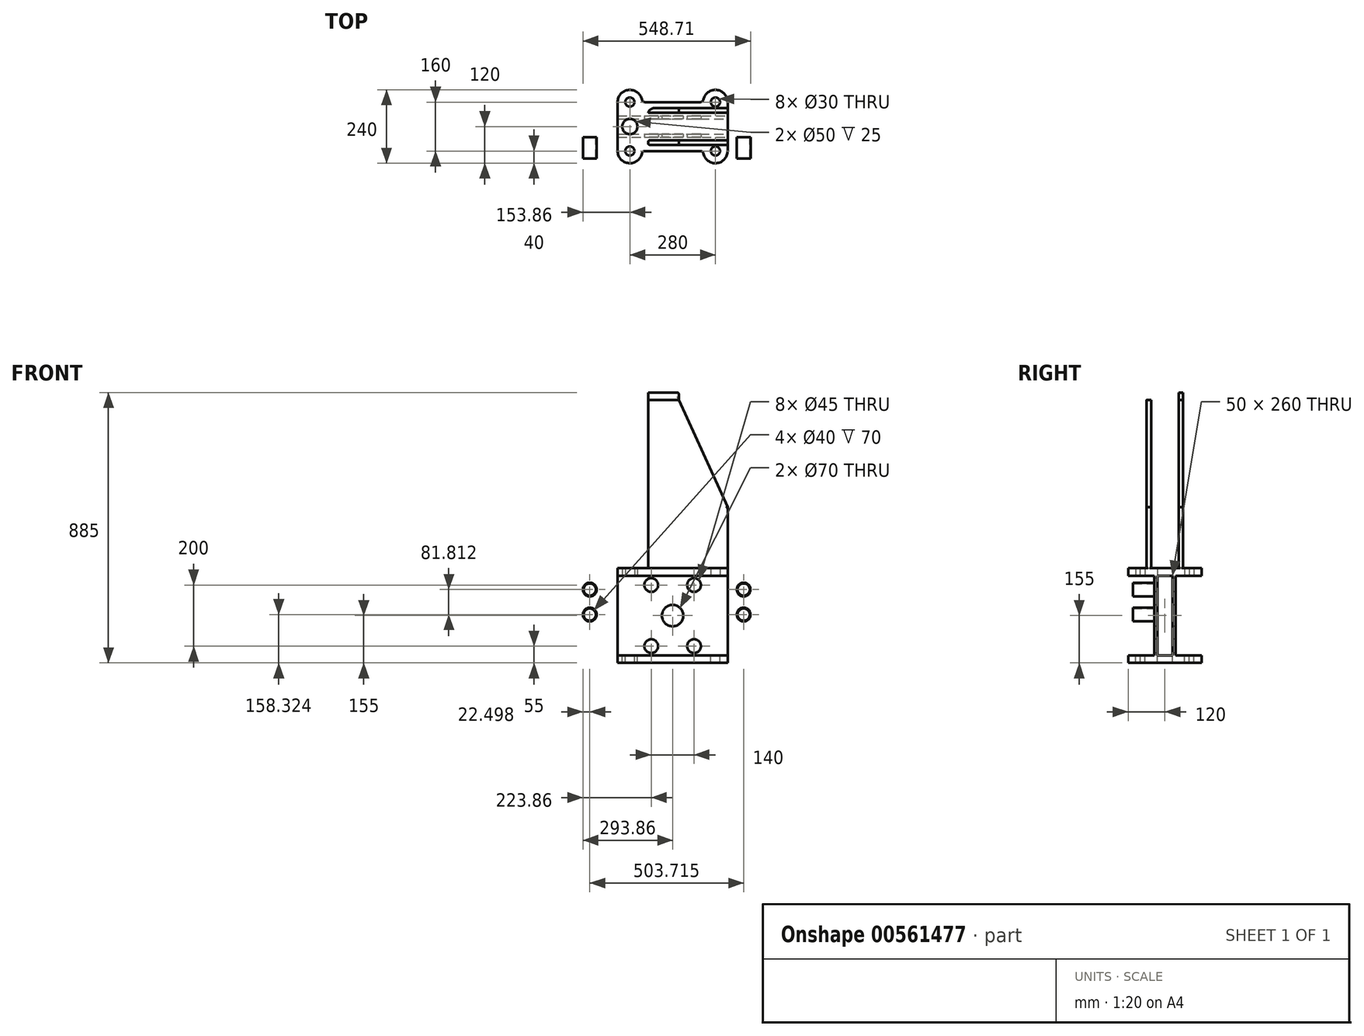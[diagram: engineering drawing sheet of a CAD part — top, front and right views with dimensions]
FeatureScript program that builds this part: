
annotation { "Feature Type Name" : "Feature", "Feature Type Description" : "" }
export const myFeature = defineFeature(function(context is Context, id is Id, definition is map)
    precondition{}
    {
        {
            var Q0;
            Q0=qCreatedBy(makeId("Top.planeOp"),FACE);
            var sketch = newSketch(context, id + "F0", { "sketchPlane" : qUnion([Q0])});
            skCircle(sketch, "E0", {"center": v(-140, 80) * mm, "radius": 40 * mm});
            skCircle(sketch, "E1", {"center": v(140, 80) * mm, "radius": 40 * mm});
            skCircle(sketch, "E2", {"center": v(-140, -80) * mm, "radius": 40 * mm});
            skCircle(sketch, "E3", {"center": v(140, -80) * mm, "radius": 40 * mm});
            skLineSegment(sketch, "E4", {"start": v(180, 80) * mm, "end": v(180, -80) * mm});
            skLineSegment(sketch, "E5", {"start": v(-180, 80) * mm, "end": v(-180, -80) * mm});
            skLineSegment(sketch, "E6", {"start": v(-100, 80) * mm, "end": v(100, 80) * mm});
            skLineSegment(sketch, "E7", {"start": v(-100, -80) * mm, "end": v(100, -80) * mm});
            skCircle(sketch, "E8", {"center": v(-140, 0) * mm, "radius": 25 * mm});
            skCircle(sketch, "E9", {"center": v(-140, 80) * mm, "radius": 15 * mm});
            skCircle(sketch, "E10", {"center": v(140, 80) * mm, "radius": 15 * mm});
            skCircle(sketch, "E11", {"center": v(-140, -80) * mm, "radius": 15 * mm});
            skCircle(sketch, "E12", {"center": v(140, -80) * mm, "radius": 15 * mm});
            skSolve(sketch);
        }
        {
            var Q0;
            {var subQ3=sQuery(id+"F0.wireOp",EDGE,"E4");Q0=makeQuery(id+"F0.imprint","IMPRINT",FACE,{"disambiguationData":[TD([[makeQuery(id+"F0.imprint","IMPRINT",EDGE,{"derivedFrom":subQ3}),-1.0]])]});}
            var Q1;
            Q1=makeQuery(id+"F0.imprint","IMPRINT",FACE,{"disambiguationData":[TD([[makeQuery(id+"F0.imprint","IMPRINT",EDGE,{"derivedFrom":sQuery(id+"F0.wireOp",EDGE,"E9")}),-1.0]])]});
            var Q2;
            Q2=makeQuery(id+"F0.imprint","IMPRINT",FACE,{"disambiguationData":[TD([[makeQuery(id+"F0.imprint","IMPRINT",EDGE,{"derivedFrom":sQuery(id+"F0.wireOp",EDGE,"E10")}),-1.0]])]});
            var Q3;
            Q3=makeQuery(id+"F0.imprint","IMPRINT",FACE,{"disambiguationData":[TD([[makeQuery(id+"F0.imprint","IMPRINT",EDGE,{"derivedFrom":sQuery(id+"F0.wireOp",EDGE,"E12")}),-1.0]])]});
            var Q4;
            Q4=makeQuery(id+"F0.imprint","IMPRINT",FACE,{"disambiguationData":[TD([[makeQuery(id+"F0.imprint","IMPRINT",EDGE,{"derivedFrom":sQuery(id+"F0.wireOp",EDGE,"E11")}),-1.0]])]});
            extrude(context, id + "F1", {"entities" : qUnion([Q0, Q1, Q2, Q3, Q4]), "depth" : 25 * mm, "offsetDistance" : 25 * mm});
        }
        {
            var Q0;
            Q0=makeQuery(id+"F1.opExtrude","SWEPT_EDGE",EDGE,{"disambiguationData":[OSD([sQuery(id+"F0.wireOp",EDGE,"E0"),sQuery(id+"F0.wireOp",EDGE,"E6")])]});
            var Q1;
            Q1=makeQuery(id+"F1.opExtrude","SWEPT_EDGE",EDGE,{"disambiguationData":[OSD([sQuery(id+"F0.wireOp",EDGE,"E1"),sQuery(id+"F0.wireOp",EDGE,"E6")])]});
            var Q2;
            Q2=makeQuery(id+"F1.opExtrude","SWEPT_EDGE",EDGE,{"disambiguationData":[OSD([sQuery(id+"F0.wireOp",EDGE,"E3"),sQuery(id+"F0.wireOp",EDGE,"E7")])]});
            var Q3;
            Q3=makeQuery(id+"F1.opExtrude","SWEPT_EDGE",EDGE,{"disambiguationData":[OSD([sQuery(id+"F0.wireOp",EDGE,"E2"),sQuery(id+"F0.wireOp",EDGE,"E7")])]});
            fillet(context, id + "F2", {"entities" : qUnion([Q0, Q1, Q2, Q3]), "radius" : 10 * mm, "tangentPropagation" : true, "allowEdgeOverflow" : false});
        }
        {
            var Q0;
            Q0=makeQuery(id+"F1.opExtrude","CAP_FACE",FACE,{"disambiguationData":[OSD([sQuery(id+"F0.wireOp",EDGE,"E0"),sQuery(id+"F0.wireOp",EDGE,"E1"),sQuery(id+"F0.wireOp",EDGE,"E2"),sQuery(id+"F0.wireOp",EDGE,"E3"),sQuery(id+"F0.wireOp",EDGE,"E4"),sQuery(id+"F0.wireOp",EDGE,"E5"),sQuery(id+"F0.wireOp",EDGE,"E6"),sQuery(id+"F0.wireOp",EDGE,"E7"),sQuery(id+"F0.wireOp",EDGE,"E8"),sQuery(id+"F0.wireOp",EDGE,"E9"),sQuery(id+"F0.wireOp",EDGE,"E10"),sQuery(id+"F0.wireOp",EDGE,"E11"),sQuery(id+"F0.wireOp",EDGE,"E12")])],"isStart":true});
            var sketch = newSketch(context, id + "F3", { "sketchPlane" : qUnion([Q0])});
            skLineSegment(sketch, "E13.bottom", {"start": v(-180, 25) * mm, "end": v(180, 25) * mm});
            skLineSegment(sketch, "E13.top", {"start": v(-180, 35) * mm, "end": v(180, 35) * mm});
            skLineSegment(sketch, "E13.left", {"start": v(-180, 25) * mm, "end": v(-180, 35) * mm});
            skLineSegment(sketch, "E13.right", {"start": v(180, 25) * mm, "end": v(180, 35) * mm});
            skLineSegment(sketch, "E14.bottom", {"start": v(-180, -25) * mm, "end": v(180, -25) * mm});
            skLineSegment(sketch, "E14.top", {"start": v(-180, -35) * mm, "end": v(180, -35) * mm});
            skLineSegment(sketch, "E14.left", {"start": v(-180, -25) * mm, "end": v(-180, -35) * mm});
            skLineSegment(sketch, "E14.right", {"start": v(180, -25) * mm, "end": v(180, -35) * mm});
            skSolve(sketch);
        }
        {
            var Q0;
            Q0=makeQuery(id+"F3.imprint","IMPRINT",FACE,{"disambiguationData":[TD([[makeQuery(id+"F3.imprint","IMPRINT",EDGE,{"derivedFrom":sQuery(id+"F3.wireOp",EDGE,"E13.top")}),-1.0]])]});
            var Q1;
            Q1=makeQuery(id+"F3.imprint","IMPRINT",FACE,{"disambiguationData":[TD([[makeQuery(id+"F3.imprint","IMPRINT",EDGE,{"derivedFrom":sQuery(id+"F3.wireOp",EDGE,"E14.top")}),1.0]])]});
            extrude(context, id + "F4", {"entities" : qUnion([Q0, Q1]), "operationType" : NewBodyOperationType.ADD, "depth" : 260 * mm, "offsetDistance" : 25 * mm});
        }
        {
            var Q0;
            Q0=makeQuery(id+"F4.opExtrude","CAP_FACE",FACE,{"disambiguationData":[OSD([sQuery(id+"F3.wireOp",EDGE,"E13.bottom"),sQuery(id+"F3.wireOp",EDGE,"E13.top"),sQuery(id+"F3.wireOp",EDGE,"E13.left"),sQuery(id+"F3.wireOp",EDGE,"E13.right")])],"isStart":false});
            var sketch = newSketch(context, id + "F5", { "sketchPlane" : qUnion([Q0])});
            skLineSegment(sketch, "E15.0", {"start": v(-180, 35) * mm, "end": v(-180, 80) * mm});
            skArc(sketch, "E16.0", {"start": v(-180, 80) * mm, "mid": v(-144.02, 119.8) * mm, "end": v(-100.8, 88) * mm});
            skLineSegment(sketch, "E17.0", {"start": v(-91.01, 80) * mm, "end": v(91.01, 80) * mm});
            skLineSegment(sketch, "E18.0.0", {"start": v(-180, 80) * mm, "end": v(-180, 35) * mm});
            skLineSegment(sketch, "E18.0.1", {"start": v(-180, 35) * mm, "end": v(180, 35) * mm});
            skLineSegment(sketch, "E18.0.2", {"start": v(180, 35) * mm, "end": v(180, 80) * mm});
            skArc(sketch, "E18.0.3", {"start": v(180, 80) * mm, "mid": v(144.02, 119.8) * mm, "end": v(100.8, 88) * mm});
            skArc(sketch, "E18.0.4", {"start": v(100.8, 88) * mm, "mid": v(97.33, 82.25) * mm, "end": v(91.01, 80) * mm});
            skLineSegment(sketch, "E18.0.5", {"start": v(91.01, 80) * mm, "end": v(-91.01, 80) * mm});
            skArc(sketch, "E18.0.6", {"start": v(-91.01, 80) * mm, "mid": v(-97.33, 82.25) * mm, "end": v(-100.8, 88) * mm});
            skArc(sketch, "E18.0.7", {"start": v(-100.8, 88) * mm, "mid": v(-144.02, 119.8) * mm, "end": v(-180, 80) * mm});
            skLineSegment(sketch, "E19.0.0", {"start": v(180, -35) * mm, "end": v(-180, -35) * mm});
            skLineSegment(sketch, "E19.0.1", {"start": v(-180, -35) * mm, "end": v(-180, -80) * mm});
            skArc(sketch, "E19.0.2", {"start": v(-180, -80) * mm, "mid": v(-144.02, -119.8) * mm, "end": v(-100.8, -88) * mm});
            skArc(sketch, "E19.0.3", {"start": v(-100.8, -88) * mm, "mid": v(-97.33, -82.25) * mm, "end": v(-91.01, -80) * mm});
            skLineSegment(sketch, "E19.0.4", {"start": v(-91.01, -80) * mm, "end": v(91.01, -80) * mm});
            skArc(sketch, "E19.0.5", {"start": v(91.01, -80) * mm, "mid": v(97.33, -82.25) * mm, "end": v(100.8, -88) * mm});
            skArc(sketch, "E19.0.6", {"start": v(100.8, -88) * mm, "mid": v(144.02, -119.8) * mm, "end": v(180, -80) * mm});
            skLineSegment(sketch, "E19.0.7", {"start": v(180, -80) * mm, "end": v(180, -35) * mm});
            skArc(sketch, "E20.0.0", {"start": v(-140, 25) * mm, "mid": v(-115, 0) * mm, "end": v(-140, -25) * mm});
            skLineSegment(sketch, "E20.0.1", {"start": v(-140, -25) * mm, "end": v(180, -25) * mm});
            skLineSegment(sketch, "E20.0.2", {"start": v(180, -25) * mm, "end": v(180, 25) * mm});
            skLineSegment(sketch, "E20.0.3", {"start": v(180, 25) * mm, "end": v(-140, 25) * mm});
            skLineSegment(sketch, "E21.0.0", {"start": v(-180, 25) * mm, "end": v(-180, -25) * mm});
            skLineSegment(sketch, "E21.0.1", {"start": v(-180, -25) * mm, "end": v(-140, -25) * mm});
            skArc(sketch, "E21.0.2", {"start": v(-140, -25) * mm, "mid": v(-165, 0) * mm, "end": v(-140, 25) * mm});
            skLineSegment(sketch, "E21.0.3", {"start": v(-140, 25) * mm, "end": v(-180, 25) * mm});
            skLineSegment(sketch, "E22.0.0", {"start": v(180, 35) * mm, "end": v(-180, 35) * mm});
            skLineSegment(sketch, "E22.0.1", {"start": v(-180, 35) * mm, "end": v(-180, 25) * mm});
            skLineSegment(sketch, "E22.0.2", {"start": v(-180, 25) * mm, "end": v(180, 25) * mm});
            skLineSegment(sketch, "E22.0.3", {"start": v(180, 25) * mm, "end": v(180, 35) * mm});
            skLineSegment(sketch, "E23.0.0", {"start": v(-180, -25) * mm, "end": v(-180, -35) * mm});
            skLineSegment(sketch, "E23.0.1", {"start": v(-180, -35) * mm, "end": v(180, -35) * mm});
            skLineSegment(sketch, "E23.0.2", {"start": v(180, -35) * mm, "end": v(180, -25) * mm});
            skLineSegment(sketch, "E23.0.3", {"start": v(180, -25) * mm, "end": v(-180, -25) * mm});
            skCircle(sketch, "E24", {"center": v(-140, 80) * mm, "radius": 15 * mm});
            skCircle(sketch, "E25", {"center": v(140, 80) * mm, "radius": 15 * mm});
            skCircle(sketch, "E26", {"center": v(140, -80) * mm, "radius": 15 * mm});
            skCircle(sketch, "E27", {"center": v(-140, -80) * mm, "radius": 15 * mm});
            skSolve(sketch);
        }
        {
            var Q0;
            Q0 = qSketchRegion(id + "F5", true);
            extrude(context, id + "F6", {"entities" : qUnion([Q0]), "operationType" : NewBodyOperationType.ADD, "depth" : 25 * mm, "offsetDistance" : 25 * mm});
        }
        {
            var Q0;
            Q0=makeQuery(id+"F4.opExtrude","SWEPT_FACE",FACE,{"disambiguationData":[OSD([sQuery(id+"F3.wireOp",EDGE,"E13.top")])]});
            var sketch = newSketch(context, id + "F7", { "sketchPlane" : qUnion([Q0])});
            skLineSegment(sketch, "E28", {"start": v(0, 0) * mm, "end": v(0, -293.43) * mm, "construction": true});
            skPoint(sketch, "E28.endSnap0", {"position": v(0, -260) * mm});
            skCircle(sketch, "E29", {"center": v(-70, -30) * mm, "radius": 22.5 * mm});
            skCircle(sketch, "E30", {"center": v(70, -30) * mm, "radius": 22.5 * mm});
            skCircle(sketch, "E31", {"center": v(-70, -230) * mm, "radius": 22.5 * mm});
            skCircle(sketch, "E32", {"center": v(70, -230) * mm, "radius": 22.5 * mm});
            skCircle(sketch, "E33", {"center": v(0, -130) * mm, "radius": 35 * mm});
            skSolve(sketch);
        }
        {
            var Q0;
            Q0=makeQuery(id+"F7.imprint","IMPRINT",FACE,{"disambiguationData":[TD([[makeQuery(id+"F7.imprint","IMPRINT",EDGE,{"derivedFrom":sQuery(id+"F7.wireOp",EDGE,"E29")}),1.0]])]});
            var Q1;
            Q1=makeQuery(id+"F7.imprint","IMPRINT",FACE,{"disambiguationData":[TD([[makeQuery(id+"F7.imprint","IMPRINT",EDGE,{"derivedFrom":sQuery(id+"F7.wireOp",EDGE,"E30")}),1.0]])]});
            var Q2;
            Q2=makeQuery(id+"F7.imprint","IMPRINT",FACE,{"disambiguationData":[TD([[makeQuery(id+"F7.imprint","IMPRINT",EDGE,{"derivedFrom":sQuery(id+"F7.wireOp",EDGE,"E33")}),1.0]])]});
            var Q3;
            Q3=makeQuery(id+"F7.imprint","IMPRINT",FACE,{"disambiguationData":[TD([[makeQuery(id+"F7.imprint","IMPRINT",EDGE,{"derivedFrom":sQuery(id+"F7.wireOp",EDGE,"E32")}),1.0]])]});
            var Q4;
            Q4=makeQuery(id+"F7.imprint","IMPRINT",FACE,{"disambiguationData":[TD([[makeQuery(id+"F7.imprint","IMPRINT",EDGE,{"derivedFrom":sQuery(id+"F7.wireOp",EDGE,"E31")}),1.0]])]});
            extrude(context, id + "F8", {"entities" : qUnion([Q0, Q1, Q2, Q3, Q4]), "operationType" : NewBodyOperationType.REMOVE, "oppositeDirection" : true, "depth" : 70 * mm, "offsetDistance" : 25 * mm});
        }
        {
            var Q0;
            Q0=makeQuery(id+"F4.opExtrude","SWEPT_FACE",FACE,{"disambiguationData":[OSD([sQuery(id+"F3.wireOp",EDGE,"E13.top")])]});
            var sketch = newSketch(context, id + "F9", { "sketchPlane" : qUnion([Q0])});
            skCircle(sketch, "E34", {"center": v(-271.36, -44.86) * mm, "radius": 22.5 * mm});
            skCircle(sketch, "E35", {"center": v(-271.36, -44.86) * mm, "radius": 20 * mm});
            skCircle(sketch, "E36", {"center": v(-271.36, -126.68) * mm, "radius": 22.5 * mm});
            skCircle(sketch, "E37", {"center": v(-271.36, -126.68) * mm, "radius": 20 * mm});
            skCircle(sketch, "E38", {"center": v(232.35, -44.86) * mm, "radius": 22.5 * mm});
            skCircle(sketch, "E39", {"center": v(232.35, -44.86) * mm, "radius": 20 * mm});
            skCircle(sketch, "E40", {"center": v(232.35, -126.68) * mm, "radius": 22.5 * mm});
            skCircle(sketch, "E41", {"center": v(232.35, -126.68) * mm, "radius": 20 * mm});
            skSolve(sketch);
        }
        {
            var Q0;
            Q0=makeQuery(id+"F9.imprint","IMPRINT",FACE,{"disambiguationData":[TD([[makeQuery(id+"F9.imprint","IMPRINT",EDGE,{"derivedFrom":sQuery(id+"F9.wireOp",EDGE,"E34")}),1.0]])]});
            var Q1;
            Q1=makeQuery(id+"F9.imprint","IMPRINT",FACE,{"disambiguationData":[TD([[makeQuery(id+"F9.imprint","IMPRINT",EDGE,{"derivedFrom":sQuery(id+"F9.wireOp",EDGE,"E36")}),1.0]])]});
            var Q2;
            Q2=makeQuery(id+"F9.imprint","IMPRINT",FACE,{"disambiguationData":[TD([[makeQuery(id+"F9.imprint","IMPRINT",EDGE,{"derivedFrom":sQuery(id+"F9.wireOp",EDGE,"E38")}),1.0]])]});
            var Q3;
            Q3=makeQuery(id+"F9.imprint","IMPRINT",FACE,{"disambiguationData":[TD([[makeQuery(id+"F9.imprint","IMPRINT",EDGE,{"derivedFrom":sQuery(id+"F9.wireOp",EDGE,"E40")}),1.0]])]});
            extrude(context, id + "F10", {"entities" : qUnion([Q0, Q1, Q2, Q3]), "depth" : 70 * mm, "offsetDistance" : 25 * mm});
        }
        {
            var Q0;
            Q0=makeQuery(id+"F1.opExtrude","CAP_FACE",FACE,{"disambiguationData":[OSD([sQuery(id+"F0.wireOp",EDGE,"E0"),sQuery(id+"F0.wireOp",EDGE,"E1"),sQuery(id+"F0.wireOp",EDGE,"E2"),sQuery(id+"F0.wireOp",EDGE,"E3"),sQuery(id+"F0.wireOp",EDGE,"E4"),sQuery(id+"F0.wireOp",EDGE,"E5"),sQuery(id+"F0.wireOp",EDGE,"E6"),sQuery(id+"F0.wireOp",EDGE,"E7"),sQuery(id+"F0.wireOp",EDGE,"E8"),sQuery(id+"F0.wireOp",EDGE,"E9"),sQuery(id+"F0.wireOp",EDGE,"E10"),sQuery(id+"F0.wireOp",EDGE,"E11"),sQuery(id+"F0.wireOp",EDGE,"E12")])],"isStart":false});
            var sketch = newSketch(context, id + "F11", { "sketchPlane" : qUnion([Q0])});
            skLineSegment(sketch, "E42.bottom", {"start": v(180, 60) * mm, "end": v(-80, 60) * mm});
            skLineSegment(sketch, "E42.top", {"start": v(180, 45) * mm, "end": v(-80, 45) * mm});
            skLineSegment(sketch, "E42.left", {"start": v(180, 60) * mm, "end": v(180, 45) * mm});
            skLineSegment(sketch, "E42.right", {"start": v(-80, 60) * mm, "end": v(-80, 45) * mm});
            skLineSegment(sketch, "E43.bottom", {"start": v(180, -60) * mm, "end": v(-80, -60) * mm});
            skLineSegment(sketch, "E43.top", {"start": v(180, -45) * mm, "end": v(-80, -45) * mm});
            skLineSegment(sketch, "E43.left", {"start": v(180, -60) * mm, "end": v(180, -45) * mm});
            skLineSegment(sketch, "E43.right", {"start": v(-80, -60) * mm, "end": v(-80, -45) * mm});
            skSolve(sketch);
        }
        {
            var Q0;
            Q0=makeQuery(id+"F11.imprint","IMPRINT",FACE,{"disambiguationData":[TD([[makeQuery(id+"F11.imprint","IMPRINT",EDGE,{"derivedFrom":sQuery(id+"F11.wireOp",EDGE,"E42.bottom")}),1.0]])]});
            var Q1;
            Q1=makeQuery(id+"F11.imprint","IMPRINT",FACE,{"disambiguationData":[TD([[makeQuery(id+"F11.imprint","IMPRINT",EDGE,{"derivedFrom":sQuery(id+"F11.wireOp",EDGE,"E43.bottom")}),-1.0]])]});
            extrude(context, id + "F12", {"entities" : qUnion([Q0, Q1]), "operationType" : NewBodyOperationType.ADD, "depth" : 550 * mm, "offsetDistance" : 25 * mm});
        }
        {
            var Q0;
            Q0=makeQuery(id+"F12.opExtrude","SWEPT_FACE",FACE,{"disambiguationData":[OSD([sQuery(id+"F11.wireOp",EDGE,"E43.bottom")])]});
            var sketch = newSketch(context, id + "F13", { "sketchPlane" : qUnion([Q0])});
            skLineSegment(sketch, "E44", {"start": v(20, 575) * mm, "end": v(180, 225) * mm});
            skSolve(sketch);
        }
        {
            var Q0;
            {var subQ0=sQuery(id+"F13.wireOp",EDGE,"E44");Q0=makeQuery(id+"F13.imprint","IMPRINT",FACE,{"disambiguationData":[TD([[makeQuery(id+"F13.imprint","IMPRINT",EDGE,{"derivedFrom":subQ0}),1.0]])]});}
            extrude(context, id + "F14", {"entities" : qUnion([Q0]), "operationType" : NewBodyOperationType.REMOVE, "endBound" : BoundingType.SYMMETRIC, "depth" : 70 * mm, "offsetDistance" : 25 * mm});
        }
        {
            var Q0;
            Q0=makeQuery(id+"F12.opExtrude","SWEPT_FACE",FACE,{"disambiguationData":[OSD([sQuery(id+"F11.wireOp",EDGE,"E42.bottom")])]});
            var sketch = newSketch(context, id + "F15", { "sketchPlane" : qUnion([Q0])});
            skLineSegment(sketch, "E45", {"start": v(-20, 575) * mm, "end": v(-180, 225) * mm});
            skSolve(sketch);
        }
        {
            var Q0;
            {var subQ0=sQuery(id+"F15.wireOp",EDGE,"E45");Q0=makeQuery(id+"F15.imprint","IMPRINT",FACE,{"disambiguationData":[TD([[makeQuery(id+"F15.imprint","IMPRINT",EDGE,{"derivedFrom":subQ0}),-1.0]])]});}
            extrude(context, id + "F16", {"entities" : qUnion([Q0]), "operationType" : NewBodyOperationType.REMOVE, "oppositeDirection" : true, "depth" : 70 * mm, "offsetDistance" : 25 * mm});
        }
        {
            var Q0;
            Q0=makeQuery(id+"F12.opExtrude","CAP_FACE",FACE,{"disambiguationData":[OSD([sQuery(id+"F11.wireOp",EDGE,"E42.bottom"),sQuery(id+"F11.wireOp",EDGE,"E42.top"),sQuery(id+"F11.wireOp",EDGE,"E42.left"),sQuery(id+"F11.wireOp",EDGE,"E42.right")])],"isStart":false});
            var sketch = newSketch(context, id + "F17", { "sketchPlane" : qUnion([Q0])});
            skLineSegment(sketch, "E46.1.0", {"start": v(-80, -60) * mm, "end": v(20, -60) * mm});
            skLineSegment(sketch, "E46.1.1", {"start": v(20, -60) * mm, "end": v(20, -45) * mm});
            skLineSegment(sketch, "E46.1.2", {"start": v(20, -45) * mm, "end": v(-80, -45) * mm});
            skLineSegment(sketch, "E46.1.3", {"start": v(-80, -45) * mm, "end": v(-80, -60) * mm});
            skLineSegment(sketch, "E46.2.0", {"start": v(180, -80) * mm, "end": v(180, -60) * mm});
            skLineSegment(sketch, "E46.2.1", {"start": v(180, -60) * mm, "end": v(-80, -60) * mm});
            skLineSegment(sketch, "E46.2.2", {"start": v(-80, -60) * mm, "end": v(-80, -45) * mm});
            skLineSegment(sketch, "E46.2.3", {"start": v(-80, -45) * mm, "end": v(180, -45) * mm});
            skLineSegment(sketch, "E46.2.4", {"start": v(180, -45) * mm, "end": v(180, 45) * mm});
            skLineSegment(sketch, "E46.2.5", {"start": v(180, 45) * mm, "end": v(-80, 45) * mm});
            skLineSegment(sketch, "E46.2.6", {"start": v(-80, 45) * mm, "end": v(-80, 60) * mm});
            skLineSegment(sketch, "E46.2.7", {"start": v(-80, 60) * mm, "end": v(180, 60) * mm});
            skLineSegment(sketch, "E46.2.8", {"start": v(180, 60) * mm, "end": v(180, 80) * mm});
            skArc(sketch, "E46.2.9", {"start": v(180, 80) * mm, "mid": v(144.02, 119.8) * mm, "end": v(100.8, 88) * mm});
            skArc(sketch, "E46.2.10", {"start": v(100.8, 88) * mm, "mid": v(97.33, 82.25) * mm, "end": v(91.01, 80) * mm});
            skLineSegment(sketch, "E46.2.11", {"start": v(91.01, 80) * mm, "end": v(-91.01, 80) * mm});
            skArc(sketch, "E46.2.12", {"start": v(-91.01, 80) * mm, "mid": v(-97.33, 82.25) * mm, "end": v(-100.8, 88) * mm});
            skArc(sketch, "E46.2.13", {"start": v(-100.8, 88) * mm, "mid": v(-144.02, 119.8) * mm, "end": v(-180, 80) * mm});
            skLineSegment(sketch, "E46.2.14", {"start": v(-180, 80) * mm, "end": v(-180, -80) * mm});
            skArc(sketch, "E46.2.15", {"start": v(-180, -80) * mm, "mid": v(-144.02, -119.8) * mm, "end": v(-100.8, -88) * mm});
            skArc(sketch, "E46.2.16", {"start": v(-100.8, -88) * mm, "mid": v(-97.33, -82.25) * mm, "end": v(-91.01, -80) * mm});
            skLineSegment(sketch, "E46.2.17", {"start": v(-91.01, -80) * mm, "end": v(91.01, -80) * mm});
            skArc(sketch, "E46.2.18", {"start": v(91.01, -80) * mm, "mid": v(97.33, -82.25) * mm, "end": v(100.8, -88) * mm});
            skArc(sketch, "E46.2.19", {"start": v(100.8, -88) * mm, "mid": v(144.02, -119.8) * mm, "end": v(180, -80) * mm});
            skLineSegment(sketch, "E47", {"start": v(20, 60) * mm, "end": v(-180, 60) * mm});
            skLineSegment(sketch, "E48", {"start": v(-180, 60) * mm, "end": v(-180, -60) * mm});
            skLineSegment(sketch, "E49", {"start": v(-180, -60) * mm, "end": v(20, -60) * mm});
            skLineSegment(sketch, "E50", {"start": v(20, 60) * mm, "end": v(20, -60) * mm});
            skCircle(sketch, "E51", {"center": v(-140, 0) * mm, "radius": 25 * mm});
            skSolve(sketch);
        }
        {
            var Q0;
            {var subQ2=sQuery(id+"F17.wireOp",EDGE,"E46.2.2");Q0=makeQuery(id+"F17.imprint","IMPRINT",FACE,{"disambiguationData":[TD([[makeQuery(id+"F17.imprint","IMPRINT",EDGE,{"derivedFrom":subQ2}),1.0]])]});}
            var Q1;
            {var subQ0=sQuery(id+"F17.wireOp",EDGE,"E46.2.6");Q1=makeQuery(id+"F17.imprint","IMPRINT",FACE,{"disambiguationData":[TD([[makeQuery(id+"F17.imprint","IMPRINT",EDGE,{"derivedFrom":subQ0}),1.0]])]});}
            var Q2;
            {var subQ0=sQuery(id+"F17.wireOp",EDGE,"E46.2.2");Q2=makeQuery(id+"F17.imprint","IMPRINT",FACE,{"disambiguationData":[TD([[makeQuery(id+"F17.imprint","IMPRINT",EDGE,{"derivedFrom":subQ0}),-1.0]])]});}
            extrude(context, id + "F18", {"entities" : qUnion([Q0, Q1, Q2]), "operationType" : NewBodyOperationType.ADD, "depth" : 25 * mm, "offsetDistance" : 25 * mm});
        }
        {
            var Q0;
            Q0=makeQuery(id+"F18.opExtrude","SWEPT_EDGE",EDGE,{"disambiguationData":[OSD([sQuery(id+"F17.wireOp",EDGE,"E46.2.14"),sQuery(id+"F17.wireOp",EDGE,"E47"),sQuery(id+"F17.wireOp",EDGE,"E48")])]});
            var Q1;
            Q1=makeQuery(id+"F18.opExtrude","SWEPT_EDGE",EDGE,{"disambiguationData":[OSD([sQuery(id+"F17.wireOp",EDGE,"E46.2.14"),sQuery(id+"F17.wireOp",EDGE,"E48"),sQuery(id+"F17.wireOp",EDGE,"E49")])]});
            fillet(context, id + "F19", {"entities" : qUnion([Q0, Q1]), "radius" : 20 * mm, "tangentPropagation" : true, "allowEdgeOverflow" : false});
        }
        {
            var Q0;
            Q0=makeQuery(id+"F18.opExtrude","CAP_EDGE",EDGE,{"disambiguationData":[OSD([sQuery(id+"F17.wireOp",EDGE,"E50")])],"isStart":false});
            var Q1;
            Q1=makeQuery(id+"F18.opExtrude","SWEPT_EDGE",EDGE,{"disambiguationData":[OSD([sQuery(id+"F17.wireOp",EDGE,"E46.2.1"),sQuery(id+"F17.wireOp",EDGE,"E49"),sQuery(id+"F17.wireOp",EDGE,"E50")])]});
            var Q2;
            Q2=makeQuery(id+"F18.opExtrude","SWEPT_EDGE",EDGE,{"disambiguationData":[OSD([sQuery(id+"F17.wireOp",EDGE,"E46.2.7"),sQuery(id+"F17.wireOp",EDGE,"E47"),sQuery(id+"F17.wireOp",EDGE,"E50")])]});
            var Q3;
            Q3=makeQuery(id+"F16.boolean.opBoolean","COPY",EDGE,{"derivedFrom":makeQuery(id+"F16.opExtrude","CAP_EDGE",EDGE,{"disambiguationData":[OSD([sQuery(id+"F15.wireOp",EDGE,"E45")])],"isStart":true})});
            var Q4;
            Q4=makeQuery(id+"F16.boolean.opBoolean","INTERSECT",EDGE,{"derivedFrom":[makeQuery(id+"F12.opExtrude","SWEPT_FACE",FACE,{"disambiguationData":[OSD([sQuery(id+"F11.wireOp",EDGE,"E42.top")])]}),makeQuery(id+"F16.opExtrude","SWEPT_FACE",FACE,{"disambiguationData":[OSD([sQuery(id+"F15.wireOp",EDGE,"E45")])]})]});
            var Q5;
            Q5=makeQuery(id+"F12.opExtrude","SWEPT_EDGE",EDGE,{"disambiguationData":[OSD([sQuery(id+"F0.wireOp",EDGE,"E4"),sQuery(id+"F11.wireOp",EDGE,"E42.top"),sQuery(id+"F11.wireOp",EDGE,"E42.left")])]});
            var Q6;
            Q6=makeQuery(id+"F12.opExtrude","SWEPT_EDGE",EDGE,{"disambiguationData":[OSD([sQuery(id+"F0.wireOp",EDGE,"E4"),sQuery(id+"F11.wireOp",EDGE,"E42.bottom"),sQuery(id+"F11.wireOp",EDGE,"E42.left")])]});
            var Q7;
            Q7=makeQuery(id+"F12.opExtrude","SWEPT_EDGE",EDGE,{"disambiguationData":[OSD([sQuery(id+"F11.wireOp",EDGE,"E42.bottom"),sQuery(id+"F11.wireOp",EDGE,"E42.right")])]});
            var Q8;
            Q8=makeQuery(id+"F12.opExtrude","SWEPT_EDGE",EDGE,{"disambiguationData":[OSD([sQuery(id+"F11.wireOp",EDGE,"E42.top"),sQuery(id+"F11.wireOp",EDGE,"E42.right")])]});
            var Q9;
            Q9=makeQuery(id+"F12.opExtrude","SWEPT_EDGE",EDGE,{"disambiguationData":[OSD([sQuery(id+"F11.wireOp",EDGE,"E43.bottom"),sQuery(id+"F11.wireOp",EDGE,"E43.right")])]});
            var Q10;
            Q10=makeQuery(id+"F12.opExtrude","SWEPT_EDGE",EDGE,{"disambiguationData":[OSD([sQuery(id+"F11.wireOp",EDGE,"E43.top"),sQuery(id+"F11.wireOp",EDGE,"E43.right")])]});
            var Q11;
            Q11=makeQuery(id+"F18.opExtrude","CAP_EDGE",EDGE,{"disambiguationData":[OSD([sQuery(id+"F17.wireOp",EDGE,"E48")])],"isStart":false});
            var Q12;
            Q12=makeQuery(id+"F18.opExtrude","CAP_EDGE",EDGE,{"disambiguationData":[OSD([sQuery(id+"F17.wireOp",EDGE,"E48")])],"isStart":true});
            var Q13;
            Q13=makeQuery(id+"F14.boolean.opBoolean","INTERSECT",EDGE,{"derivedFrom":[makeQuery(id+"F12.opExtrude","SWEPT_FACE",FACE,{"disambiguationData":[OSD([sQuery(id+"F11.wireOp",EDGE,"E43.bottom")])]}),makeQuery(id+"F14.opExtrude","SWEPT_FACE",FACE,{"disambiguationData":[OSD([sQuery(id+"F13.wireOp",EDGE,"E44")])]})]});
            var Q14;
            Q14=makeQuery(id+"F12.opExtrude","SWEPT_EDGE",EDGE,{"disambiguationData":[OSD([sQuery(id+"F0.wireOp",EDGE,"E4"),sQuery(id+"F11.wireOp",EDGE,"E43.bottom"),sQuery(id+"F11.wireOp",EDGE,"E43.left")])]});
            var Q15;
            Q15=makeQuery(id+"F12.opExtrude","SWEPT_EDGE",EDGE,{"disambiguationData":[OSD([sQuery(id+"F0.wireOp",EDGE,"E4"),sQuery(id+"F11.wireOp",EDGE,"E43.top"),sQuery(id+"F11.wireOp",EDGE,"E43.left")])]});
            var Q16;
            Q16=makeQuery(id+"F14.boolean.opBoolean","INTERSECT",EDGE,{"derivedFrom":[makeQuery(id+"F12.opExtrude","SWEPT_FACE",FACE,{"disambiguationData":[OSD([sQuery(id+"F11.wireOp",EDGE,"E43.top")])]}),makeQuery(id+"F14.opExtrude","SWEPT_FACE",FACE,{"disambiguationData":[OSD([sQuery(id+"F13.wireOp",EDGE,"E44")])]})]});
            fillet(context, id + "F20", {"entities" : qUnion([Q0, Q1, Q2, Q3, Q4, Q5, Q6, Q7, Q8, Q9, Q10, Q11, Q12, Q13, Q14, Q15, Q16]), "radius" : 5 * mm, "tangentPropagation" : true, "allowEdgeOverflow" : false});
        }
    });
